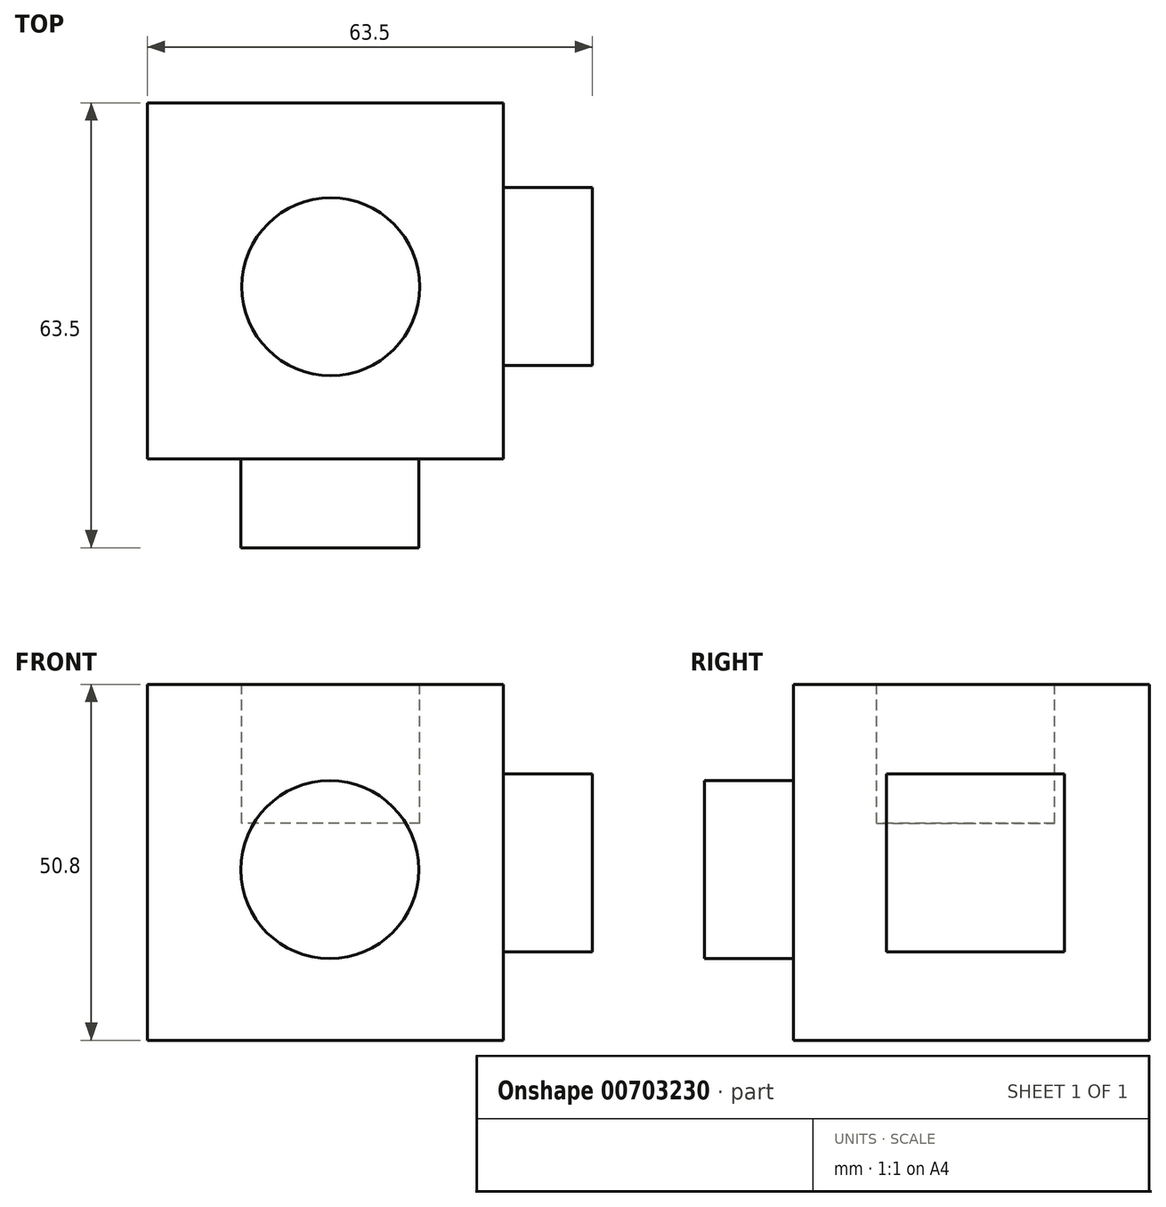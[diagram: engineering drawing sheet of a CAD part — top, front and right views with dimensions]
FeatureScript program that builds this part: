
annotation { "Feature Type Name" : "Feature", "Feature Type Description" : "" }
export const myFeature = defineFeature(function(context is Context, id is Id, definition is map)
    precondition{}
    {
        {
            var Q0;
            Q0=qCreatedBy(makeId("Front.planeOp"),FACE);
            var sketch = newSketch(context, id + "F0", { "sketchPlane" : qUnion([Q0])});
            skLineSegment(sketch, "E0.bottom", {"start": v(-31.42, 26.45) * mm, "end": v(19.38, 26.45) * mm});
            skLineSegment(sketch, "E0.top", {"start": v(-31.42, -24.35) * mm, "end": v(19.38, -24.35) * mm});
            skLineSegment(sketch, "E0.left", {"start": v(-31.42, 26.45) * mm, "end": v(-31.42, -24.35) * mm});
            skLineSegment(sketch, "E0.right", {"start": v(19.38, 26.45) * mm, "end": v(19.38, -24.35) * mm});
            skSolve(sketch);
        }
        {
            var Q0;
            Q0 = qSketchRegion(id + "F0", true);
            extrude(context, id + "F1", {"entities" : qUnion([Q0]), "depth" : 50.8 * mm, "offsetDistance" : 25.4 * mm});
        }
        {
            var Q0;
            Q0=makeQuery(id+"F1.opExtrude","CAP_FACE",FACE,{"disambiguationData":[OSD([sQuery(id+"F0.wireOp",EDGE,"E0.bottom"),sQuery(id+"F0.wireOp",EDGE,"E0.top"),sQuery(id+"F0.wireOp",EDGE,"E0.left"),sQuery(id+"F0.wireOp",EDGE,"E0.right")])],"isStart":false});
            var sketch = newSketch(context, id + "F2", { "sketchPlane" : qUnion([Q0])});
            skCircle(sketch, "E1", {"center": v(-5.4, 0) * mm, "radius": 12.7 * mm});
            skSolve(sketch);
        }
        {
            var Q0;
            Q0 = qSketchRegion(id + "F2", true);
            extrude(context, id + "F3", {"entities" : qUnion([Q0]), "operationType" : NewBodyOperationType.ADD, "depth" : 12.7 * mm, "offsetDistance" : 25.4 * mm});
        }
        {
            var Q0;
            Q0=makeQuery(id+"F1.opExtrude","SWEPT_FACE",FACE,{"disambiguationData":[OSD([sQuery(id+"F0.wireOp",EDGE,"E0.right")])]});
            var sketch = newSketch(context, id + "F4", { "sketchPlane" : qUnion([Q0])});
            skLineSegment(sketch, "E2.bottom", {"start": v(-37.53, 13.66) * mm, "end": v(-12.13, 13.66) * mm});
            skLineSegment(sketch, "E2.top", {"start": v(-37.53, -11.74) * mm, "end": v(-12.13, -11.74) * mm});
            skLineSegment(sketch, "E2.left", {"start": v(-37.53, 13.66) * mm, "end": v(-37.53, -11.74) * mm});
            skLineSegment(sketch, "E2.right", {"start": v(-12.13, 13.66) * mm, "end": v(-12.13, -11.74) * mm});
            skSolve(sketch);
        }
        {
            var Q0;
            Q0 = qSketchRegion(id + "F4", true);
            extrude(context, id + "F5", {"entities" : qUnion([Q0]), "operationType" : NewBodyOperationType.ADD, "depth" : 12.7 * mm, "offsetDistance" : 25.4 * mm});
        }
        {
            var Q0;
            Q0=makeQuery(id+"F1.opExtrude","SWEPT_FACE",FACE,{"disambiguationData":[OSD([sQuery(id+"F0.wireOp",EDGE,"E0.bottom")])]});
            var sketch = newSketch(context, id + "F6", { "sketchPlane" : qUnion([Q0])});
            skCircle(sketch, "E3", {"center": v(-5.25, -26.26) * mm, "radius": 12.7 * mm});
            skSolve(sketch);
        }
        {
            var Q0;
            Q0 = qSketchRegion(id + "F6", true);
            extrude(context, id + "F7", {"entities" : qUnion([Q0]), "operationType" : NewBodyOperationType.REMOVE, "oppositeDirection" : true, "depth" : 19.8 * mm, "offsetDistance" : 25.4 * mm});
        }
    });
